# Revit family: LM0156831_Mueble  Plus 120 Cm
name_source: partatom
category: Specialty Equipment
units: mm (PartAtom-declared; Revit-internal decimal feet)

## family parameters
Always vertical = Yes
Cut with Voids When Loaded = No
Part Type = Normal
Room Calculation Point = No
Round Connector Dimension = Use Diameter
Shared = No
Work Plane-Based = No

## types (1)
- LM0156831_Mueble  Plus 120 Cm
    Alto = 425 mm  [stored 1.39436 ft]
    Altura Lavamanos = 150 mm
    Ancho = 1196 mm  [stored 3.92388 ft]
    Ancho Lavamanos = 460 mm  [stored 1.50919 ft]
    Canto = PVC rígido 22 mm de calibre.
    Creado por = IDD
    Densidad = 25mm 597 kg./m^3.
    Dimensiones generales del producto = 16,73” x 47,09” x 19,69” (425 x 1196 x 500 mm).
    Fecha de creación = 30/07/2020
    Manufacturer = Corona
    Material = Corona_Porcelana_Sanitaria
    Material 2 = Corona_Madera_Aglomerada_Duna
    Material 3 = Corona_Madera_Onix
    Model = Mueble Plus 120cm
    Peso Bruto aprox = 82,5 lb (37,4 kg).
    Peso Neto aprox = 71,2 lb (32,3 kg).
    Profundida Lavamanos = 376 mm  [stored 1.2336 ft]
    Profundidad = 500 mm  [stored 1.64042 ft]
    Resistencia a la humedad = 8%.
    Resistencia al Rayado = 700 ciclos.

note: [stored X ft] marks values corroborated as IEEE doubles in the binary element streams (Revit-internal decimal feet)

## geometry (parser evidence)
native form markers: Sweep x2
no freeform markers — native parametric forms only
